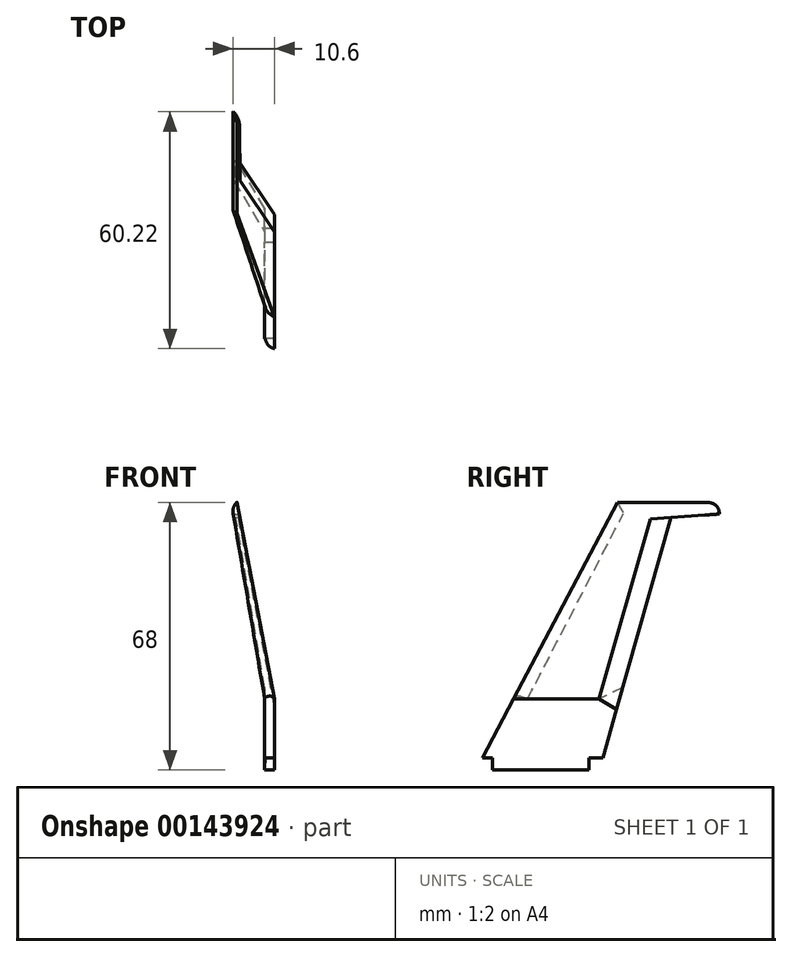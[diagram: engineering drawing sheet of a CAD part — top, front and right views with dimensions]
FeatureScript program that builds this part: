
annotation { "Feature Type Name" : "Feature", "Feature Type Description" : "" }
export const myFeature = defineFeature(function(context is Context, id is Id, definition is map)
    precondition{}
    {
        {
            var Q0;
            Q0=qCreatedBy(makeId("Top.planeOp"),FACE);
            var sketch = newSketch(context, id + "F0", { "sketchPlane" : qUnion([Q0])});
            skLineSegment(sketch, "E0", {"start": v(0, 0) * mm, "end": v(-2.5, 0) * mm});
            skLineSegment(sketch, "E1", {"start": v(-2.5, 0) * mm, "end": v(-2.5, 24.5) * mm});
            skLineSegment(sketch, "E2", {"start": v(-2.5, 24.5) * mm, "end": v(0, 24.5) * mm});
            skLineSegment(sketch, "E3", {"start": v(0, 24.5) * mm, "end": v(0, 0) * mm});
            skSolve(sketch);
        }
        {
            var Q0;
            Q0 = qSketchRegion(id + "F0", true);
            extrude(context, id + "F1", {"entities" : qUnion([Q0]), "depth" : 3 * mm});
        }
        {
            var Q0;
            Q0=makeQuery(id+"F1.opExtrude","SWEPT_FACE",FACE,{"disambiguationData":[OSD([sQuery(id+"F0.wireOp",EDGE,"E0")])]});
            var sketch = newSketch(context, id + "F2", { "sketchPlane" : qUnion([Q0])});
            skLineSegment(sketch, "E4", {"start": v(0, 3) * mm, "end": v(0, 18) * mm});
            skLineSegment(sketch, "E5", {"start": v(0, 3) * mm, "end": v(-2.5, 3) * mm});
            skLineSegment(sketch, "E6", {"start": v(-2.5, 3) * mm, "end": v(-2.5, 18) * mm});
            skLineSegment(sketch, "E7", {"start": v(-2.5, 18) * mm, "end": v(0, 18) * mm});
            skLineSegment(sketch, "E8", {"start": v(0, 18) * mm, "end": v(-9.54, 68) * mm});
            skLineSegment(sketch, "E9", {"start": v(-2.5, 18) * mm, "end": v(-11.04, 68) * mm});
            skLineSegment(sketch, "E10.trimOffspring", {"start": v(-9.54, 68) * mm, "end": v(-11.04, 68) * mm});
            skSolve(sketch);
        }
        {
            var Q0;
            Q0 = qSketchRegion(id + "F2", true);
            extrude(context, id + "F3", {"entities" : qUnion([Q0]), "operationType" : NewBodyOperationType.ADD, "oppositeDirection" : true, "depth" : 120 * mm, "symmetric" : true});
        }
        {
            var Q0;
            Q0=qCreatedBy(makeId("Right.planeOp"),FACE);
            var sketch = newSketch(context, id + "F4", { "sketchPlane" : qUnion([Q0])});
            skLineSegment(sketch, "E11", {"start": v(-2.64, 3) * mm, "end": v(31.64, 68) * mm});
            skLineSegment(sketch, "E12", {"start": v(31.64, 68) * mm, "end": v(57.58, 68) * mm});
            skLineSegment(sketch, "E13", {"start": v(57.58, 65) * mm, "end": v(45.33, 64.16) * mm});
            skLineSegment(sketch, "E14", {"start": v(45.33, 64.16) * mm, "end": v(28, 3) * mm});
            skLineSegment(sketch, "E15", {"start": v(57.58, 68) * mm, "end": v(57.58, 65) * mm});
            skLineSegment(sketch, "E16", {"start": v(28, 3) * mm, "end": v(67.76, 3) * mm});
            skLineSegment(sketch, "E17", {"start": v(67.76, 3) * mm, "end": v(67.76, 72.01) * mm});
            skLineSegment(sketch, "E18", {"start": v(67.76, 72.01) * mm, "end": v(0, 72.01) * mm});
            skLineSegment(sketch, "E19", {"start": v(-2.64, 3) * mm, "end": v(-63.96, 3) * mm});
            skLineSegment(sketch, "E20", {"start": v(-63.96, 3) * mm, "end": v(-63.96, 72.01) * mm});
            skLineSegment(sketch, "E21", {"start": v(-63.96, 72.01) * mm, "end": v(0, 72.01) * mm});
            skPoint(sketch, "E22.orphan", {"position": v(0, 3) * mm});
            skSolve(sketch);
        }
        {
            var Q0;
            Q0 = qSketchRegion(id + "F4", true);
            extrude(context, id + "F5", {"entities" : qUnion([Q0]), "operationType" : NewBodyOperationType.REMOVE, "oppositeDirection" : true, "depth" : 25 * mm});
        }
        {
            var Q0;
            Q0=makeQuery(id+"F5.boolean.opBoolean","INTERSECT",EDGE,{"derivedFrom":[makeQuery(id+"F3.opExtrude","SWEPT_FACE",FACE,{"disambiguationData":[OSD([sQuery(id+"F2.wireOp",EDGE,"E9")])]}),makeQuery(id+"F5.opExtrude","SWEPT_FACE",FACE,{"disambiguationData":[OSD([sQuery(id+"F4.wireOp",EDGE,"E14")])]})]});
            var Q1;
            Q1=makeQuery(id+"F5.boolean.opBoolean","INTERSECT",EDGE,{"derivedFrom":[makeQuery(id+"F3.opExtrude","SWEPT_FACE",FACE,{"disambiguationData":[OSD([sQuery(id+"F2.wireOp",EDGE,"E8")])]}),makeQuery(id+"F5.opExtrude","SWEPT_FACE",FACE,{"disambiguationData":[OSD([sQuery(id+"F4.wireOp",EDGE,"E14")])]})]});
            chamfer(context, id + "F6", {"entities" : qUnion([Q0, Q1]), "chamferType" : ChamferType.TWO_OFFSETS, "width1" : 5 * mm, "oppositeDirection" : false, "width2" : .5 * mm, "tangentPropagation" : true});
        }
        {
            var Q0;
            Q0=makeQuery(id+"F5.boolean.opBoolean","INTERSECT",EDGE,{"derivedFrom":[makeQuery(id+"F3.opExtrude","SWEPT_FACE",FACE,{"disambiguationData":[OSD([sQuery(id+"F2.wireOp",EDGE,"E9")])]}),makeQuery(id+"F5.opExtrude","SWEPT_FACE",FACE,{"disambiguationData":[OSD([sQuery(id+"F4.wireOp",EDGE,"E11")])]})]});
            var Q1;
            Q1=makeQuery(id+"F3.opExtrude","SWEPT_EDGE",EDGE,{"disambiguationData":[OSD([sQuery(id+"F2.wireOp",EDGE,"E9"),sQuery(id+"F2.wireOp",EDGE,"E10.trimOffspring")])]});
            var Q2;
            Q2=makeQuery(id+"F5.boolean.opBoolean","INTERSECT",EDGE,{"derivedFrom":[makeQuery(id+"F3.boolean.opBoolean","MERGE",FACE,{"derivedFrom":[makeQuery(id+"F1.opExtrude","SWEPT_FACE",FACE,{"disambiguationData":[OSD([sQuery(id+"F0.wireOp",EDGE,"E1")])]}),makeQuery(id+"F3.opExtrude","SWEPT_FACE",FACE,{"disambiguationData":[OSD([sQuery(id+"F2.wireOp",EDGE,"E6")])]})]}),makeQuery(id+"F5.opExtrude","SWEPT_FACE",FACE,{"disambiguationData":[OSD([sQuery(id+"F4.wireOp",EDGE,"E11")])]})]});
            fillet(context, id + "F7", {"entities" : qUnion([Q0, Q1, Q2]), "radius" : 3 * mm, "tangentPropagation" : true, "allowEdgeOverflow" : false});
        }
        {
            var Q0;
            Q0=makeQuery(id+"F7.opFillet","BLEND_EDGE",EDGE,{"blendedFrom":[makeQuery(id+"F3.opExtrude","SWEPT_EDGE",EDGE,{"disambiguationData":[OSD([sQuery(id+"F2.wireOp",EDGE,"E8"),sQuery(id+"F2.wireOp",EDGE,"E10.trimOffspring")])]}),makeQuery(id+"F5.boolean.opBoolean","COPY",FACE,{"derivedFrom":makeQuery(id+"F5.opExtrude","SWEPT_FACE",FACE,{"disambiguationData":[OSD([sQuery(id+"F4.wireOp",EDGE,"E15")])]})})],"blendedInto":[makeQuery(id+"F5.boolean.opBoolean","COPY",FACE,{"derivedFrom":makeQuery(id+"F5.opExtrude","SWEPT_FACE",FACE,{"disambiguationData":[OSD([sQuery(id+"F4.wireOp",EDGE,"E15")])]})})]});
            var Q1;
            Q1=makeQuery(id+"F5.boolean.opBoolean","INTERSECT",EDGE,{"derivedFrom":[makeQuery(id+"F3.opExtrude","SWEPT_FACE",FACE,{"disambiguationData":[OSD([sQuery(id+"F2.wireOp",EDGE,"E8")])]}),makeQuery(id+"F5.opExtrude","SWEPT_FACE",FACE,{"disambiguationData":[OSD([sQuery(id+"F4.wireOp",EDGE,"E15")])]})]});
            fillet(context, id + "F8", {"entities" : qUnion([Q0, Q1]), "radius" : 5 * mm, "tangentPropagation" : true, "allowEdgeOverflow" : false});
        }
    });
